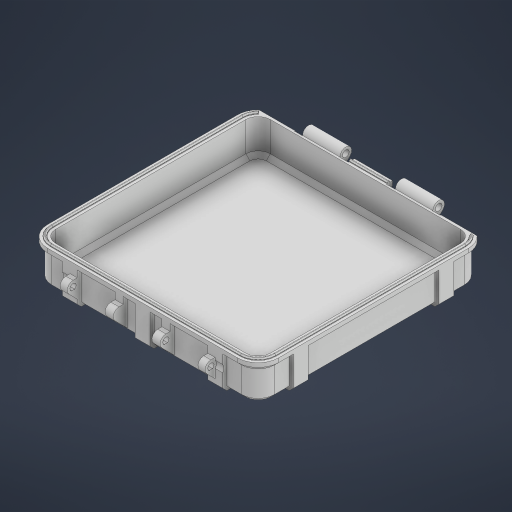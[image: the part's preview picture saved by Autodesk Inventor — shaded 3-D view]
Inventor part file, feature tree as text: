
AUTODESK INVENTOR PART (.ipt)
format: ipt  version: 2024 (Build 280153000, 153)  size: 871,936 bytes
history: native  units: mm
features: extrude x13, projected_geometry x11, sketch x8, other x6, fillet x2, chamfer x2, mirror x2, shell x1, sweep x1
ambient origin geometry x8: Origin, YZ Plane, XZ Plane, XY Plane, X Axis, Y Axis, Z Axis, Center Point
bodies: Body1 (feature_tree)
feature tree (46):
  other  "Těleso1"
  extrude  "vyska"  Depth=109.0mm
  fillet  "Zaobleni_rohu"  Radius=109.0mm
  shell  "tloustka_sten"  Thickness=18.5mm
  extrude  "vyztuhy"  Depth=8.0mm
  chamfer  "Zkoseni_spodku"  Distance=2.0mm
  sketch  "Náčrt4"
  sketch  "Náčrt3"
  sweep  "tesnici_drazka"
  chamfer  "tesnici_drazka-zkoseni"  Distance=7.266667mm
  sketch  "Náčrt16"
  extrude  "Vysunutí23"  Depth=2.0mm
  extrude  "Vysunutí24"  Depth=30.0mm TaperAngle=0.0deg
  extrude  "Vysunutí25"  Depth=2.0mm TaperAngle=45.0deg
  extrude  "Vysunutí26"  Depth=1.4mm
  extrude  "Vysunutí27"  TaperAngle=0.0deg  [1 undecoded]
  extrude  "Vysunutí28"  Depth=2.0mm TaperAngle=45.0deg
  extrude  "Vysunutí29"  Depth=3.1mm
  mirror  "Zrcadlit4"
  other  "latch-main_nacrt"
  extrude  "Vysunutí14"  Depth=8.2mm
  extrude  "Vysunutí12"  Depth=4.05mm
  other  "Pracovní rovina3"
  extrude  "Vysunutí15"  Depth=2.75mm
  extrude  "Vysunutí16"  Depth=1.5mm
  mirror  "latch-zrcadleni"
  fillet  "Zaoblení2"  Radius=5.75mm
  other  "velikost"
  other  "vyztuhy-velikost"
  projected_geometry  "Promítnutá smyčka1"
  projected_geometry  "Promítnutá smyčka2"
  projected_geometry  "Promítnutá smyčka16"
  sketch  "Náčrt10"
  projected_geometry  "Promítnutá smyčka17"
  sketch  "Náčrt12"
  projected_geometry  "Promítnutá smyčka18"
  other  "Pracovní rovina4"
  projected_geometry  "Promítnutá smyčka24"
  sketch  "Náčrt17"
  projected_geometry  "Promítnutá smyčka25"
  projected_geometry  "Promítnutá smyčka26"
  projected_geometry  "Promítnutá smyčka27"
  sketch  "Náčrt18"
  projected_geometry  "Promítnutá smyčka28"
  sketch  "Náčrt19"
  projected_geometry  "Promítnutá smyčka29"
note: 1 required parameter value undecoded (feature->parameter linkage not recoverable at this tier; creation-order binding heuristic only, values carry confidence <= 0.55)
